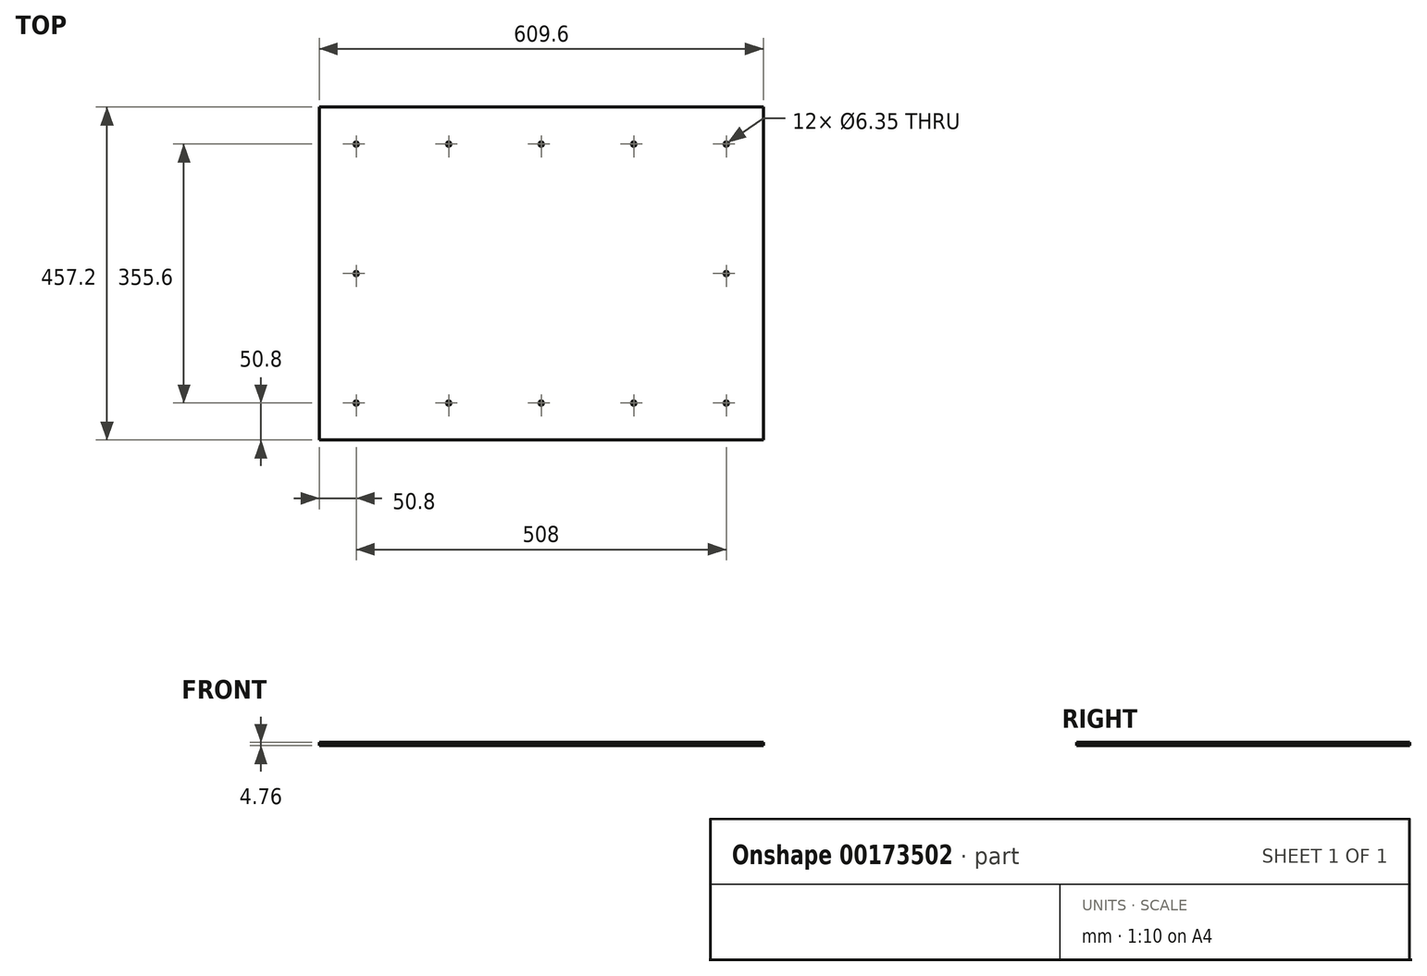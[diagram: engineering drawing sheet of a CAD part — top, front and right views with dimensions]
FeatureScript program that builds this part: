
annotation { "Feature Type Name" : "Feature", "Feature Type Description" : "" }
export const myFeature = defineFeature(function(context is Context, id is Id, definition is map)
    precondition{}
    {
        {
            var Q0;
            Q0=qCreatedBy(makeId("Top.planeOp"),FACE);
            var sketch = newSketch(context, id + "F0", { "sketchPlane" : qUnion([Q0])});
            skLineSegment(sketch, "E0.bottom", {"start": v(304.8, -228.6) * mm, "end": v(-304.8, -228.6) * mm});
            skLineSegment(sketch, "E0.top", {"start": v(304.8, 228.6) * mm, "end": v(-304.8, 228.6) * mm});
            skLineSegment(sketch, "E0.left", {"start": v(304.8, -228.6) * mm, "end": v(304.8, 228.6) * mm});
            skLineSegment(sketch, "E0.right", {"start": v(-304.8, -228.6) * mm, "end": v(-304.8, 228.6) * mm});
            skPoint(sketch, "E0.middle", {"position": v(0, 0) * mm});
            skCircle(sketch, "E1", {"center": v(-254, 177.8) * mm, "radius": 3.18 * mm});
            skCircle(sketch, "E2", {"center": v(-254, 0) * mm, "radius": 3.18 * mm});
            skCircle(sketch, "E3.1.0.0", {"center": v(-127, 177.8) * mm, "radius": 3.18 * mm});
            skCircle(sketch, "E3.2.0.0", {"center": v(0, 177.8) * mm, "radius": 3.18 * mm});
            skCircle(sketch, "E3.3.0.0", {"center": v(127, 177.8) * mm, "radius": 3.18 * mm});
            skCircle(sketch, "E3.4.0.0", {"center": v(254, 177.8) * mm, "radius": 3.18 * mm});
            skCircle(sketch, "E4.1.0.0", {"center": v(254, 0) * mm, "radius": 3.18 * mm});
            skCircle(sketch, "E5", {"center": v(-254, -177.8) * mm, "radius": 3.18 * mm});
            skCircle(sketch, "E6.1.0.0", {"center": v(-127, -177.8) * mm, "radius": 3.18 * mm});
            skCircle(sketch, "E6.2.0.0", {"center": v(0, -177.8) * mm, "radius": 3.18 * mm});
            skCircle(sketch, "E6.3.0.0", {"center": v(127, -177.8) * mm, "radius": 3.18 * mm});
            skCircle(sketch, "E6.4.0.0", {"center": v(254, -177.8) * mm, "radius": 3.18 * mm});
            skSolve(sketch);
        }
        {
            var Q0;
            Q0 = qSketchRegion(id + "F0", true);
            extrude(context, id + "F1", {"entities" : qUnion([Q0]), "depth" : 4.76 * mm});
        }
    });
